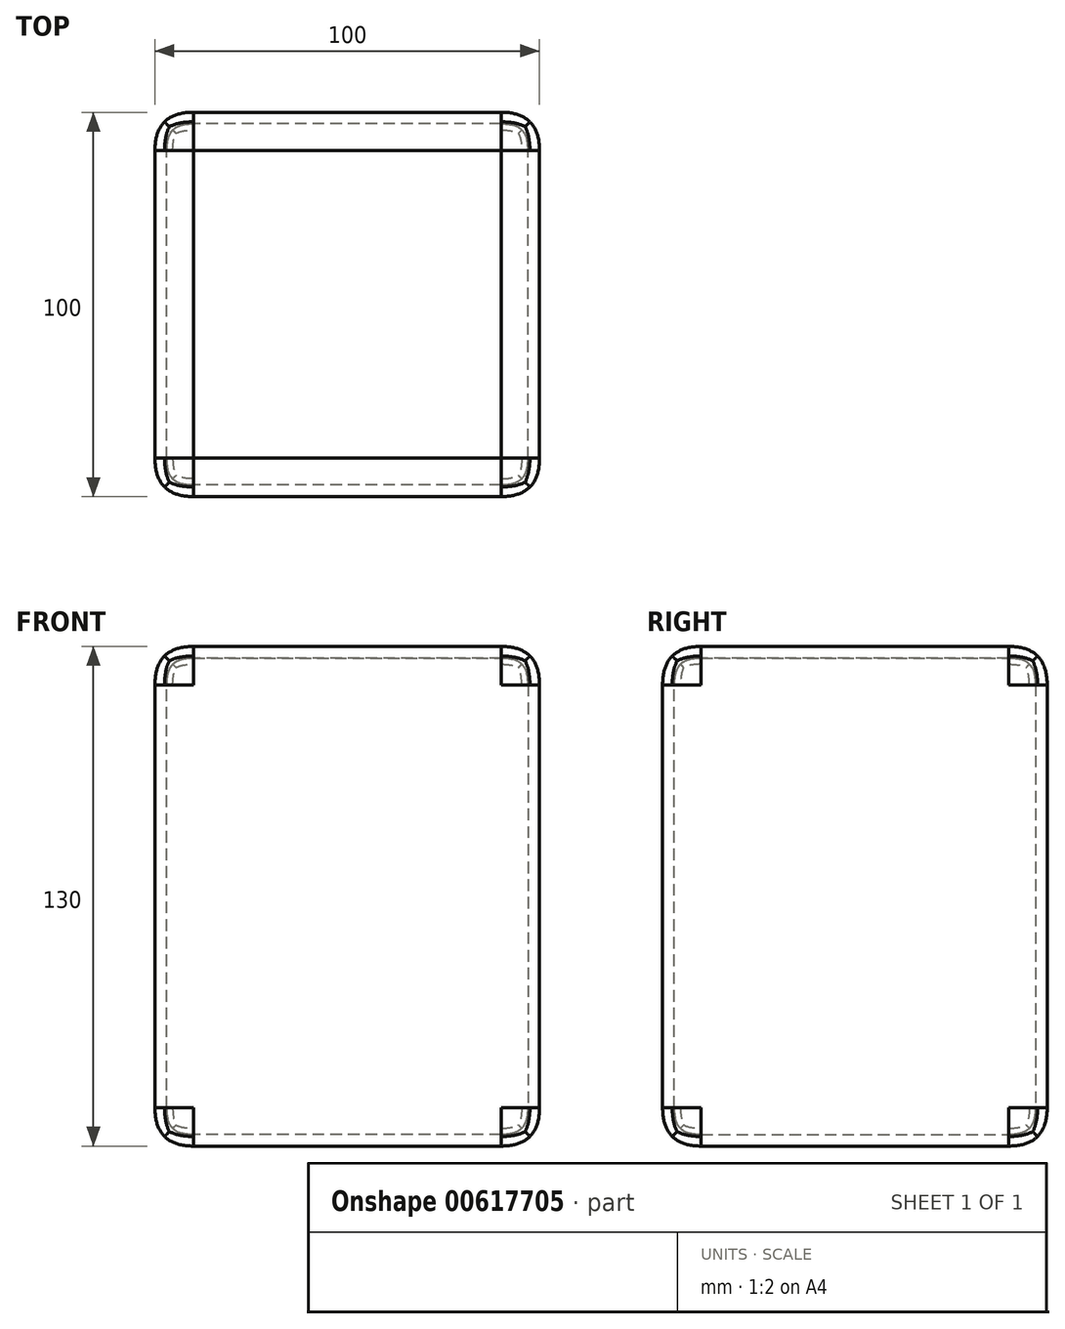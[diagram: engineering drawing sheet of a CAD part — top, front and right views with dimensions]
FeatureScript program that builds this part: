
annotation { "Feature Type Name" : "Feature", "Feature Type Description" : "" }
export const myFeature = defineFeature(function(context is Context, id is Id, definition is map)
    precondition{}
    {
        {
            var Q0;
            Q0=qCreatedBy(makeId("Top.planeOp"),FACE);
            var sketch = newSketch(context, id + "F0", { "sketchPlane" : qUnion([Q0])});
            skLineSegment(sketch, "E0.bottom", {"start": v(50, -50) * mm, "end": v(-50, -50) * mm});
            skLineSegment(sketch, "E0.top", {"start": v(50, 50) * mm, "end": v(-50, 50) * mm});
            skLineSegment(sketch, "E0.left", {"start": v(50, -50) * mm, "end": v(50, 50) * mm});
            skLineSegment(sketch, "E0.right", {"start": v(-50, -50) * mm, "end": v(-50, 50) * mm});
            skPoint(sketch, "E0.middle", {"position": v(0, 0) * mm});
            skSolve(sketch);
        }
        {
            var Q0;
            Q0 = qSketchRegion(id + "F0", true);
            extrude(context, id + "F1", {"entities" : qUnion([Q0]), "depth" : 130 * mm, "offsetDistance" : 25.4 * mm});
        }
        {
            var Q0;
            Q0=makeQuery(id+"F1.opExtrude","CAP_FACE",FACE,{"disambiguationData":[OSD([sQuery(id+"F0.wireOp",EDGE,"E0.bottom"),sQuery(id+"F0.wireOp",EDGE,"E0.top"),sQuery(id+"F0.wireOp",EDGE,"E0.left"),sQuery(id+"F0.wireOp",EDGE,"E0.right")])],"isStart":true});
            var Q1;
            Q1=makeQuery(id+"F1.opExtrude","CAP_FACE",FACE,{"disambiguationData":[OSD([sQuery(id+"F0.wireOp",EDGE,"E0.bottom"),sQuery(id+"F0.wireOp",EDGE,"E0.top"),sQuery(id+"F0.wireOp",EDGE,"E0.left"),sQuery(id+"F0.wireOp",EDGE,"E0.right")])],"isStart":false});
            var Q2;
            Q2=makeQuery(id+"F1.opExtrude","SWEPT_FACE",FACE,{"disambiguationData":[OSD([sQuery(id+"F0.wireOp",EDGE,"E0.left")])]});
            var Q3;
            Q3=makeQuery(id+"F1.opExtrude","SWEPT_FACE",FACE,{"disambiguationData":[OSD([sQuery(id+"F0.wireOp",EDGE,"E0.right")])]});
            fillet(context, id + "F2", {"entities" : qUnion([Q0, Q1, Q2, Q3]), "radius" : 10 * mm, "tangentPropagation" : true, "rho" : .5, "crossSection" : FilletCrossSection.CONIC, "allowEdgeOverflow" : false});
        }
        {
            var Q0;
            Q0=makeQuery(id+"F1.opExtrude","CAP_FACE",FACE,{"disambiguationData":[OSD([sQuery(id+"F0.wireOp",EDGE,"E0.bottom"),sQuery(id+"F0.wireOp",EDGE,"E0.top"),sQuery(id+"F0.wireOp",EDGE,"E0.left"),sQuery(id+"F0.wireOp",EDGE,"E0.right")])],"isStart":false});
            shell(context, id + "F3", {"entities" : qUnion([Q0]), "thickness" : 3 * mm});
        }
    });
